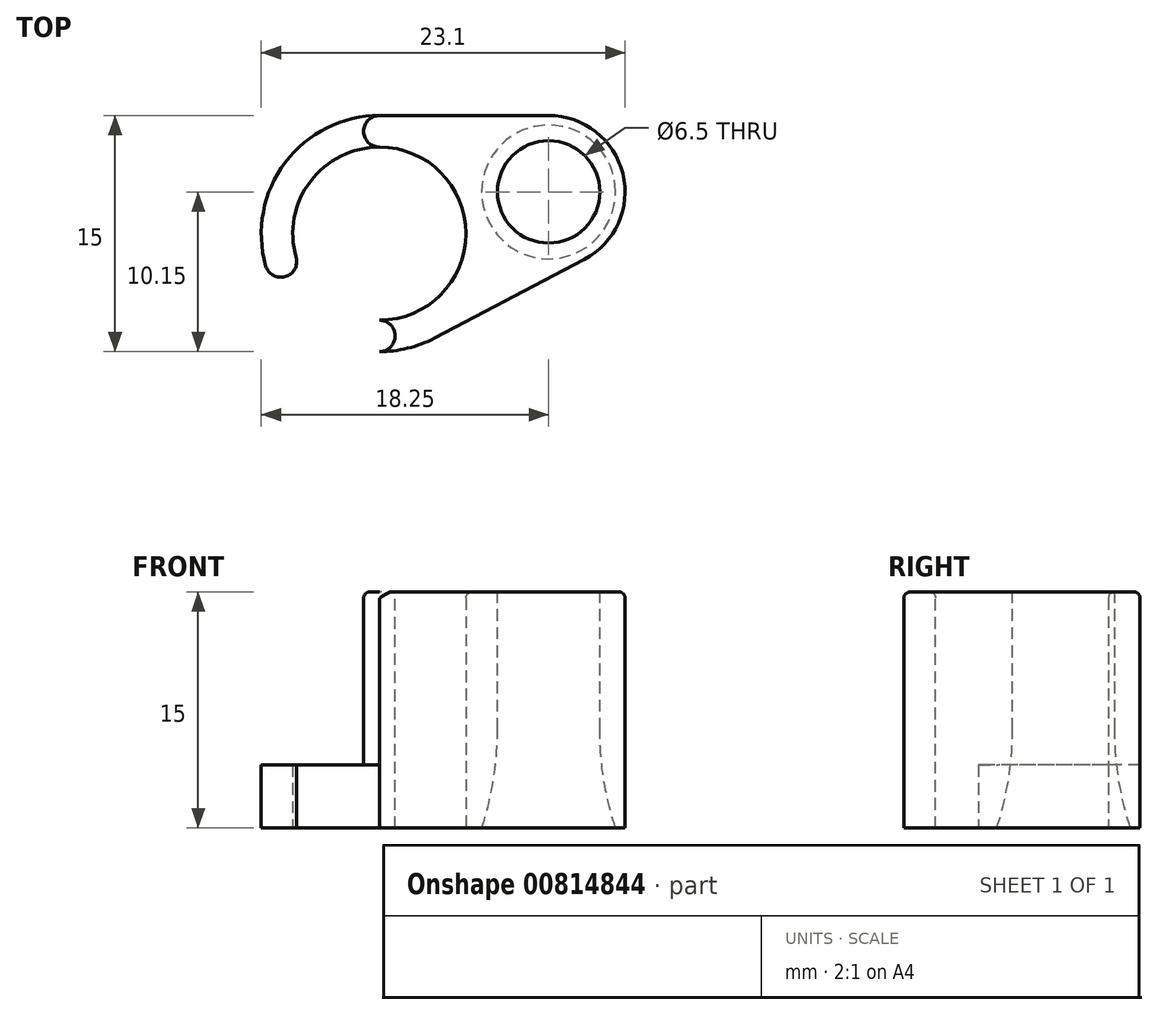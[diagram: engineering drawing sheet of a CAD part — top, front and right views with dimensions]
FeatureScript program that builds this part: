
annotation { "Feature Type Name" : "Feature", "Feature Type Description" : "" }
export const myFeature = defineFeature(function(context is Context, id is Id, definition is map)
    precondition{}
    {
        {
            var Q0;
            Q0=qCreatedBy(makeId("Top.planeOp"),FACE);
            var sketch = newSketch(context, id + "F0", { "sketchPlane" : qUnion([Q0])});
            skCircle(sketch, "E0", {"center": v(0, 0) * mm, "radius": 5.5 * mm});
            skLineSegment(sketch, "E1.bottom", {"start": v(7.5, -2.77) * mm, "end": v(-7.5, -2.77) * mm});
            skLineSegment(sketch, "E1.top", {"start": v(7.5, 7.5) * mm, "end": v(-7.5, 7.5) * mm});
            skLineSegment(sketch, "E1.left", {"start": v(7.5, -2.77) * mm, "end": v(7.5, 7.5) * mm});
            skLineSegment(sketch, "E1.right", {"start": v(-7.5, -2.77) * mm, "end": v(-7.5, 7.5) * mm});
            skPoint(sketch, "E1.middle", {"position": v(0, 2.36) * mm});
            skLineSegment(sketch, "E2", {"start": v(-4.75, -2.77) * mm, "end": v(-4.75, -2.77) * mm});
            skLineSegment(sketch, "E3", {"start": v(4.75, -2.77) * mm, "end": v(4.75, -2.77) * mm});
            skCircle(sketch, "E4", {"center": v(0, 0) * mm, "radius": 7.5 * mm});
            skSolve(sketch);
        }
        {
            var Q0;
            {var subQ0=sQuery(id+"F0.wireOp",EDGE,"E1.left");var subQ1=sQuery(id+"F0.wireOp",EDGE,"E1.top");var subQ2=makeQuery(id+"F0.imprint","INTERSECT",VERTEX,{"derivedFrom":[subQ1,subQ0]});Q0=makeQuery(id+"F0.imprint","IMPRINT",FACE,{"disambiguationData":[TD([[makeQuery(id+"F0.imprint","IMPRINT",EDGE,{"disambiguationData":[TD([[subQ2,-1.0]])],"derivedFrom":subQ1}),1.0]])]});}
            var Q1;
            {var subQ1=sQuery(id+"F0.wireOp",EDGE,"E1.bottom");var subQ3=sQuery(id+"F0.wireOp",EDGE,"E0");var subQ8=makeQuery(id+"F0.imprint","INTERSECT",VERTEX,{"disambiguationData":[OD(0.0)],"derivedFrom":[subQ3,subQ1]});Q1=makeQuery(id+"F0.imprint","IMPRINT",FACE,{"disambiguationData":[TD([[makeQuery(id+"F0.imprint","IMPRINT",EDGE,{"disambiguationData":[TD([[subQ8,-1.0]])],"derivedFrom":subQ3}),-1.0]])]});}
            extrude(context, id + "F1", {"entities" : qUnion([Q0, Q1]), "depth" : 4 * mm, "offsetDistance" : 25 * mm});
        }
        {
            var Q0;
            Q0=makeQuery(id+"F1.opExtrude","CAP_FACE",FACE,{"disambiguationData":[OSD([sQuery(id+"F0.wireOp",EDGE,"E0"),sQuery(id+"F0.wireOp",EDGE,"E1.bottom"),sQuery(id+"F0.wireOp",EDGE,"E1.top"),sQuery(id+"F0.wireOp",EDGE,"E1.left"),sQuery(id+"F0.wireOp",EDGE,"E1.right"),sQuery(id+"F0.wireOp",EDGE,"E2"),sQuery(id+"F0.wireOp",EDGE,"E3")])],"isStart":false});
            var sketch = newSketch(context, id + "F2", { "sketchPlane" : qUnion([Q0])});
            skLineSegment(sketch, "E5", {"start": v(0, 5.5) * mm, "end": v(0, 7.5) * mm, "construction": true});
            skCircle(sketch, "E6", {"center": v(0, 6.5) * mm, "radius": 1 * mm});
            skSolve(sketch);
        }
        {
            var Q0;
            Q0 = qSketchRegion(id + "F2", true);
            var Q1;
            {var subQ9=sQuery(id+"F2.wireOp",EDGE,"EDuwXjKC-1GRe-A8US-xxkb-FmC4uoNKhDB8");Q1=makeQuery(id+"F2.imprint","IMPRINT",FACE,{"disambiguationData":[TD([[makeQuery(id+"F2.imprint","IMPRINT",EDGE,{"derivedFrom":subQ9}),1.0]])]});}
            var Q2;
            {var subQ1=sQuery(id+"F0.wireOp",EDGE,"E1.top");var subQ2=makeQuery(id+"F1.opExtrude","CAP_EDGE",EDGE,{"disambiguationData":[OSD([subQ1])],"isStart":false});Q2=makeQuery(id+"F2.imprint","IMPRINT",FACE,{"disambiguationData":[TD([[makeQuery(id+"F2.imprint","IMPRINT",EDGE,{"derivedFrom":subQ2}),1.0]])]});}
            extrude(context, id + "F3", {"entities" : qUnion([Q0, Q1, Q2]), "operationType" : NewBodyOperationType.ADD, "depth" : 11 * mm, "offsetDistance" : 25 * mm});
        }
        {
            var Q0;
            Q0=makeQuery(id+"F3.opExtrude","CAP_FACE",FACE,{"disambiguationData":[OSD([sQuery(id+"F0.wireOp",EDGE,"E0"),sQuery(id+"F0.wireOp",EDGE,"E1.bottom"),sQuery(id+"F0.wireOp",EDGE,"E1.top"),sQuery(id+"F0.wireOp",EDGE,"E1.left"),sQuery(id+"F0.wireOp",EDGE,"E3"),sQuery(id+"F2.wireOp",EDGE,"EDuwXjKC-1GRe-A8US-xxkb-FmC4uoNKhDB8")])],"isStart":false});
            var sketch = newSketch(context, id + "F4", { "sketchPlane" : qUnion([Q0])});
            skCircle(sketch, "E7", {"center": v(10.75, 2.65) * mm, "radius": 3.25 * mm});
            skCircle(sketch, "E8", {"center": v(10.75, 2.65) * mm, "radius": 4.85 * mm});
            skCircle(sketch, "E9.0", {"center": v(0, 0) * mm, "radius": 5.5 * mm});
            skLineSegment(sketch, "E10", {"start": v(7.5, 7.5) * mm, "end": v(21.28, 7.5) * mm, "construction": true});
            skLineSegment(sketch, "E11", {"start": v(7.5, 7.5) * mm, "end": v(10.75, 7.5) * mm});
            skLineSegment(sketch, "E12", {"start": v(3.49, -6.64) * mm, "end": v(13, -1.64) * mm});
            skCircle(sketch, "E13", {"center": v(0, 0) * mm, "radius": 7.5 * mm});
            skCircle(sketch, "E14", {"center": v(0, -6.5) * mm, "radius": 1 * mm});
            skSolve(sketch);
        }
        {
            var Q0;
            {var subQ0=sQuery(id+"F4.wireOp",EDGE,"E7");Q0=makeQuery(id+"F4.imprint","IMPRINT",FACE,{"disambiguationData":[TD([[makeQuery(id+"F4.imprint","IMPRINT",EDGE,{"derivedFrom":subQ0}),-1.0]])]});}
            var Q1;
            {var subQ0=sQuery(id+"F4.wireOp",EDGE,"E8");var subQ1=makeQuery(id+"F3.opExtrude","CAP_EDGE",EDGE,{"disambiguationData":[OSD([sQuery(id+"F0.wireOp",EDGE,"E1.left")])],"isStart":false});var subQ2=makeQuery(id+"F4.imprint","INTERSECT",VERTEX,{"disambiguationData":[OD(0.0)],"derivedFrom":[subQ1,subQ0]});Q1=makeQuery(id+"F4.imprint","IMPRINT",FACE,{"disambiguationData":[TD([[makeQuery(id+"F4.imprint","IMPRINT",EDGE,{"disambiguationData":[TD([[subQ2,1.0]])],"derivedFrom":subQ0}),1.0]])]});}
            var Q2;
            {var subQ0=sQuery(id+"F4.wireOp",EDGE,"E8");var subQ1=makeQuery(id+"F3.opExtrude","CAP_EDGE",EDGE,{"disambiguationData":[OSD([sQuery(id+"F0.wireOp",EDGE,"E1.left")])],"isStart":false});var subQ2=makeQuery(id+"F4.imprint","INTERSECT",VERTEX,{"disambiguationData":[OD(0.0)],"derivedFrom":[subQ1,subQ0]});Q2=makeQuery(id+"F4.imprint","IMPRINT",FACE,{"disambiguationData":[TD([[makeQuery(id+"F4.imprint","IMPRINT",EDGE,{"disambiguationData":[TD([[subQ2,-1.0]])],"derivedFrom":subQ0}),1.0]])]});}
            var Q3;
            {var subQ0=sQuery(id+"F4.wireOp",EDGE,"E11");Q3=makeQuery(id+"F4.imprint","IMPRINT",FACE,{"disambiguationData":[TD([[makeQuery(id+"F4.imprint","IMPRINT",EDGE,{"derivedFrom":subQ0}),-1.0]])]});}
            var Q4;
            {var subQ0=sQuery(id+"F4.wireOp",EDGE,"E12");var subQ1=sQuery(id+"F4.wireOp",EDGE,"E8");var subQ2=makeQuery(id+"F4.imprint","INTERSECT",VERTEX,{"derivedFrom":[subQ1,subQ0]});Q4=makeQuery(id+"F4.imprint","IMPRINT",FACE,{"disambiguationData":[TD([[makeQuery(id+"F4.imprint","IMPRINT",EDGE,{"disambiguationData":[TD([[subQ2,1.0]])],"derivedFrom":subQ1}),-1.0]])]});}
            var Q5;
            {var subQ1=makeQuery(id+"F3.opExtrude","CAP_EDGE",EDGE,{"disambiguationData":[OSD([sQuery(id+"F0.wireOp",EDGE,"E3")])],"isStart":false});Q5=makeQuery(id+"F4.imprint","IMPRINT",FACE,{"disambiguationData":[TD([[makeQuery(id+"F4.imprint","IMPRINT",EDGE,{"derivedFrom":subQ1}),-1.0]])]});}
            var Q6;
            {var subQ0=sQuery(id+"F4.wireOp",EDGE,"E9.0");var subQ1=makeQuery(id+"F3.opExtrude","CAP_EDGE",EDGE,{"disambiguationData":[OSD([sQuery(id+"F0.wireOp",EDGE,"E1.bottom")])],"isStart":false});var subQ2=makeQuery(id+"F4.imprint","INTERSECT",VERTEX,{"derivedFrom":[subQ1,subQ0]});Q6=makeQuery(id+"F4.imprint","IMPRINT",FACE,{"disambiguationData":[TD([[makeQuery(id+"F4.imprint","IMPRINT",EDGE,{"disambiguationData":[TD([[subQ2,1.0]])],"derivedFrom":subQ0}),-1.0]])]});}
            var Q7;
            {var subQ0=sQuery(id+"F4.wireOp",EDGE,"E14");var subQ2=makeQuery(id+"F4.imprint","INTERSECT",VERTEX,{"derivedFrom":[sQuery(id+"F4.wireOp",EDGE,"E9.0"),subQ0]});Q7=makeQuery(id+"F4.imprint","IMPRINT",FACE,{"disambiguationData":[TD([[makeQuery(id+"F4.imprint","IMPRINT",EDGE,{"disambiguationData":[TD([[subQ2,1.0]])],"derivedFrom":subQ0}),-1.0]])]});}
            var Q8;
            Q8=makeQuery(id+"F1.opExtrude","CAP_FACE",FACE,{"disambiguationData":[OSD([sQuery(id+"F0.wireOp",EDGE,"E0"),sQuery(id+"F0.wireOp",EDGE,"E1.bottom"),sQuery(id+"F0.wireOp",EDGE,"E1.top"),sQuery(id+"F0.wireOp",EDGE,"E1.left"),sQuery(id+"F0.wireOp",EDGE,"E1.right"),sQuery(id+"F0.wireOp",EDGE,"E2"),sQuery(id+"F0.wireOp",EDGE,"E3")])],"isStart":true});
            extrude(context, id + "F5", {"entities" : qUnion([Q0, Q1, Q2, Q3, Q4, Q5, Q6, Q7]), "operationType" : NewBodyOperationType.ADD, "endBound" : BoundingType.UP_TO_SURFACE, "oppositeDirection" : true, "depth" : 10 * mm, "endBoundEntityFace" : qUnion([Q8]), "offsetDistance" : 25 * mm});
        }
        {
            var Q0;
            Q0=makeQuery(id+"F1.opExtrude","SWEPT_EDGE",EDGE,{"disambiguationData":[OSD([sQuery(id+"F0.wireOp",EDGE,"E1.bottom"),sQuery(id+"F0.wireOp",EDGE,"E1.right")])]});
            var Q1;
            Q1=makeQuery(id+"F1.opExtrude","SWEPT_EDGE",EDGE,{"disambiguationData":[OSD([sQuery(id+"F0.wireOp",EDGE,"E1.bottom"),sQuery(id+"F0.wireOp",EDGE,"E2")])]});
            var Q2;
            Q2=makeQuery(id+"F3.opExtrude","SWEPT_EDGE",EDGE,{"disambiguationData":[OSD([sQuery(id+"F0.wireOp",EDGE,"E0"),sQuery(id+"F2.wireOp",EDGE,"EDuwXjKC-1GRe-A8US-xxkb-FmC4uoNKhDB8")])]});
            var Q3;
            Q3=makeQuery(id+"F3.opExtrude","SWEPT_EDGE",EDGE,{"disambiguationData":[OSD([sQuery(id+"F0.wireOp",EDGE,"E1.top"),sQuery(id+"F2.wireOp",EDGE,"EDuwXjKC-1GRe-A8US-xxkb-FmC4uoNKhDB8")])]});
            fillet(context, id + "F6", {"entities" : qUnion([Q0, Q1, Q2, Q3]), "radius" : 1 * mm, "tangentPropagation" : true, "allowEdgeOverflow" : false});
        }
        {
            var Q0;
            Q0=makeQuery(id+"F5.opExtrude","CAP_EDGE",EDGE,{"disambiguationData":[OSD([sQuery(id+"F4.wireOp",EDGE,"E12")])],"isStart":true});
            fillet(context, id + "F7", {"entities" : qUnion([Q0]), "radius" : 0.4 * mm, "tangentPropagation" : true, "allowEdgeOverflow" : false});
        }
        {
            var Q0;
            Q0=makeQuery(id+"F5.opExtrude","CAP_EDGE",EDGE,{"disambiguationData":[OSD([sQuery(id+"F4.wireOp",EDGE,"E7")])],"isStart":false});
            chamfer(context, id + "F8", {"entities" : qUnion([Q0]), "width" : 1 * mm, "tangentPropagation" : true});
        }
        {
            var Q0;
            {var subQ0=sQuery(id+"F4.wireOp",EDGE,"E7");Q0=makeQuery(id+"F8.opChamfer","BLEND_EDGE",EDGE,{"blendedFrom":[makeQuery(id+"F5.opExtrude","CAP_EDGE",EDGE,{"disambiguationData":[OSD([subQ0])],"isStart":false}),makeQuery(id+"F5.opExtrude","SWEPT_FACE",FACE,{"disambiguationData":[OSD([subQ0])]})],"blendedInto":[makeQuery(id+"F5.opExtrude","SWEPT_FACE",FACE,{"disambiguationData":[OSD([subQ0])]})]});}
            fillet(context, id + "F9", {"entities" : qUnion([Q0]), "radius" : 20 * mm, "tangentPropagation" : true, "allowEdgeOverflow" : false});
        }
    });
